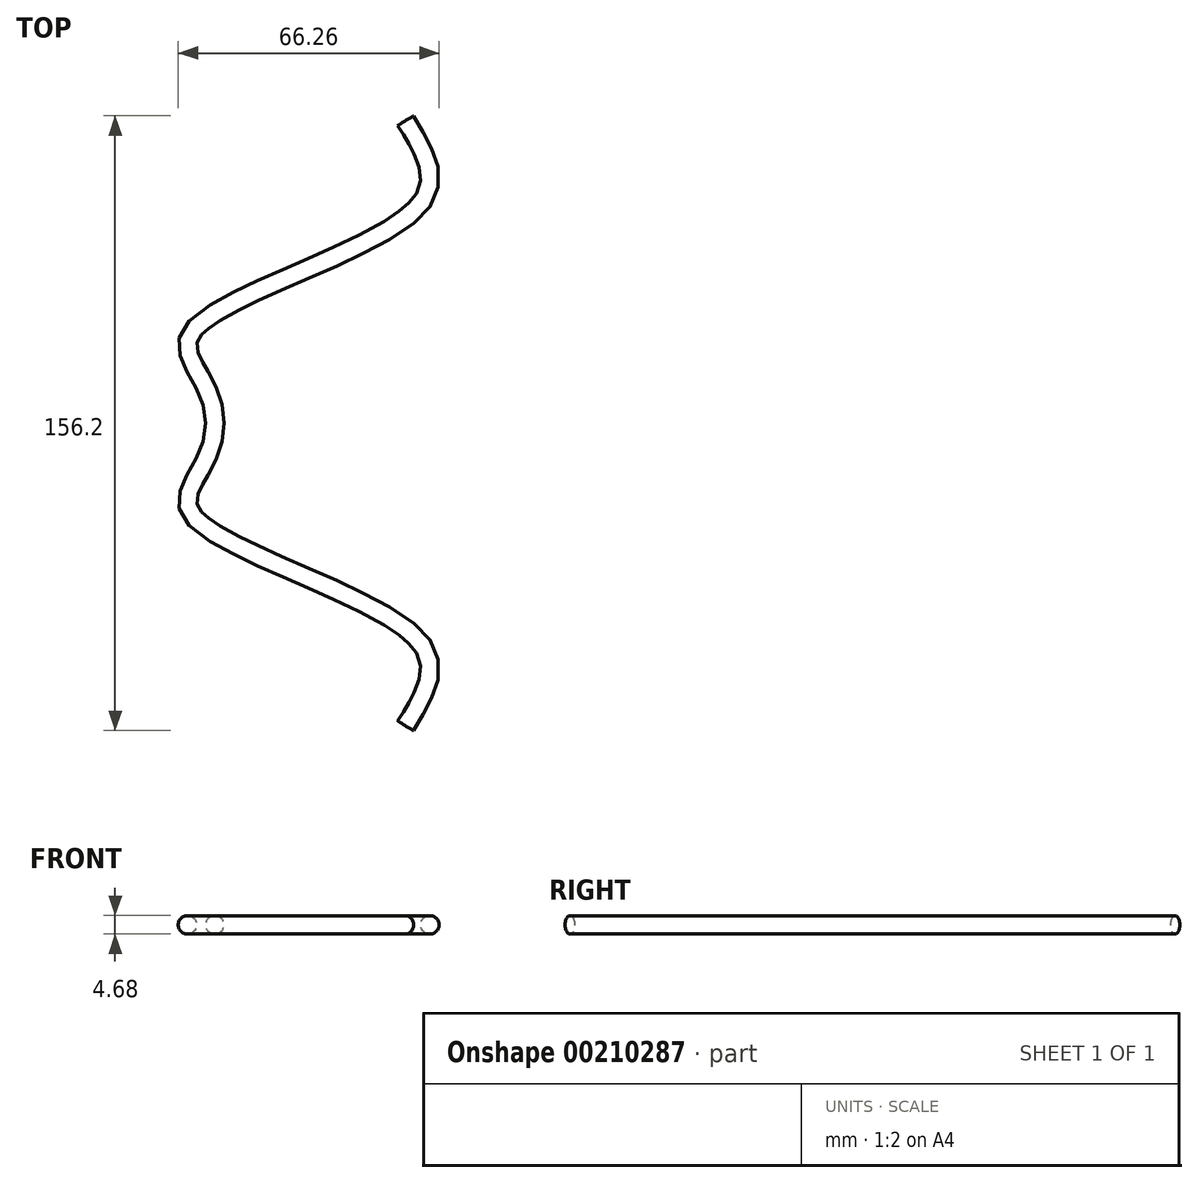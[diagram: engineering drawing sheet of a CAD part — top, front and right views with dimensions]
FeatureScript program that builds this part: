
annotation { "Feature Type Name" : "Feature", "Feature Type Description" : "" }
export const myFeature = defineFeature(function(context is Context, id is Id, definition is map)
    precondition{}
    {
        {
            var Q0;
            Q0=qCreatedBy(makeId("Top.planeOp"),FACE);
            var sketch = newSketch(context, id + "F0", { "sketchPlane" : qUnion([Q0])});
            skFitSpline(sketch, "E0", {"points": [v(0, 0) * mm, v(-6.22, 22.47) * mm, v(52.07, 55.48) * mm, v(48.48, 76.89) * mm], "startDerivative": vector(0, 119.05) * mm, "endDerivative": vector(-50.48, 83.48) * mm});
            skLineSegment(sketch, "E1", {"start": v(0, 0) * mm, "end": v(0, 10.84) * mm, "construction": true});
            skSolve(sketch);
        }
        {
            var Q0;
            Q0=qCreatedBy(makeId("Front.planeOp"),FACE);
            var sketch = newSketch(context, id + "F1", { "sketchPlane" : qUnion([Q0])});
            skCircle(sketch, "E2", {"center": v(0, 0) * mm, "radius": 2.34 * mm});
            skSolve(sketch);
        }
        {
            var Q0;
            Q0=makeQuery(id+"F1.imprint","IMPRINT",FACE,{"disambiguationData":[TD([[makeQuery(id+"F1.imprint","IMPRINT",EDGE,{"derivedFrom":sQuery(id+"F1.wireOp",EDGE,"E2")}),1.0]])]});
            var Q1;
            Q1=sQuery(id+"F0.wireOp",EDGE,"E0");
            sweep(context, id + "F2", {"profiles" : qUnion([Q0]), "path" : qUnion([Q1])});
        }
        {
            var Q0;
            Q0=makeQuery(id+"F2.opSweep","SWEPT_BODY",BODY,{"disambiguationData":[OSD([sQuery(id+"F0.wireOp",EDGE,"E0"),sQuery(id+"F1.wireOp",EDGE,"E2")])]});
            var Q1;
            Q1=makeQuery(id+"F2.opSweep","CAP_FACE",FACE,{"disambiguationData":[OSD([sQuery(id+"F0.wireOp",VERTEX,"E0.start"),sQuery(id+"F1.wireOp",EDGE,"E2")])],"isStart":true});
            mirror(context, id + "F3", {"operationType" : NewBodyOperationType.ADD, "entities" : qUnion([Q0]), "mirrorPlane" : qUnion([Q1])});
        }
    });
